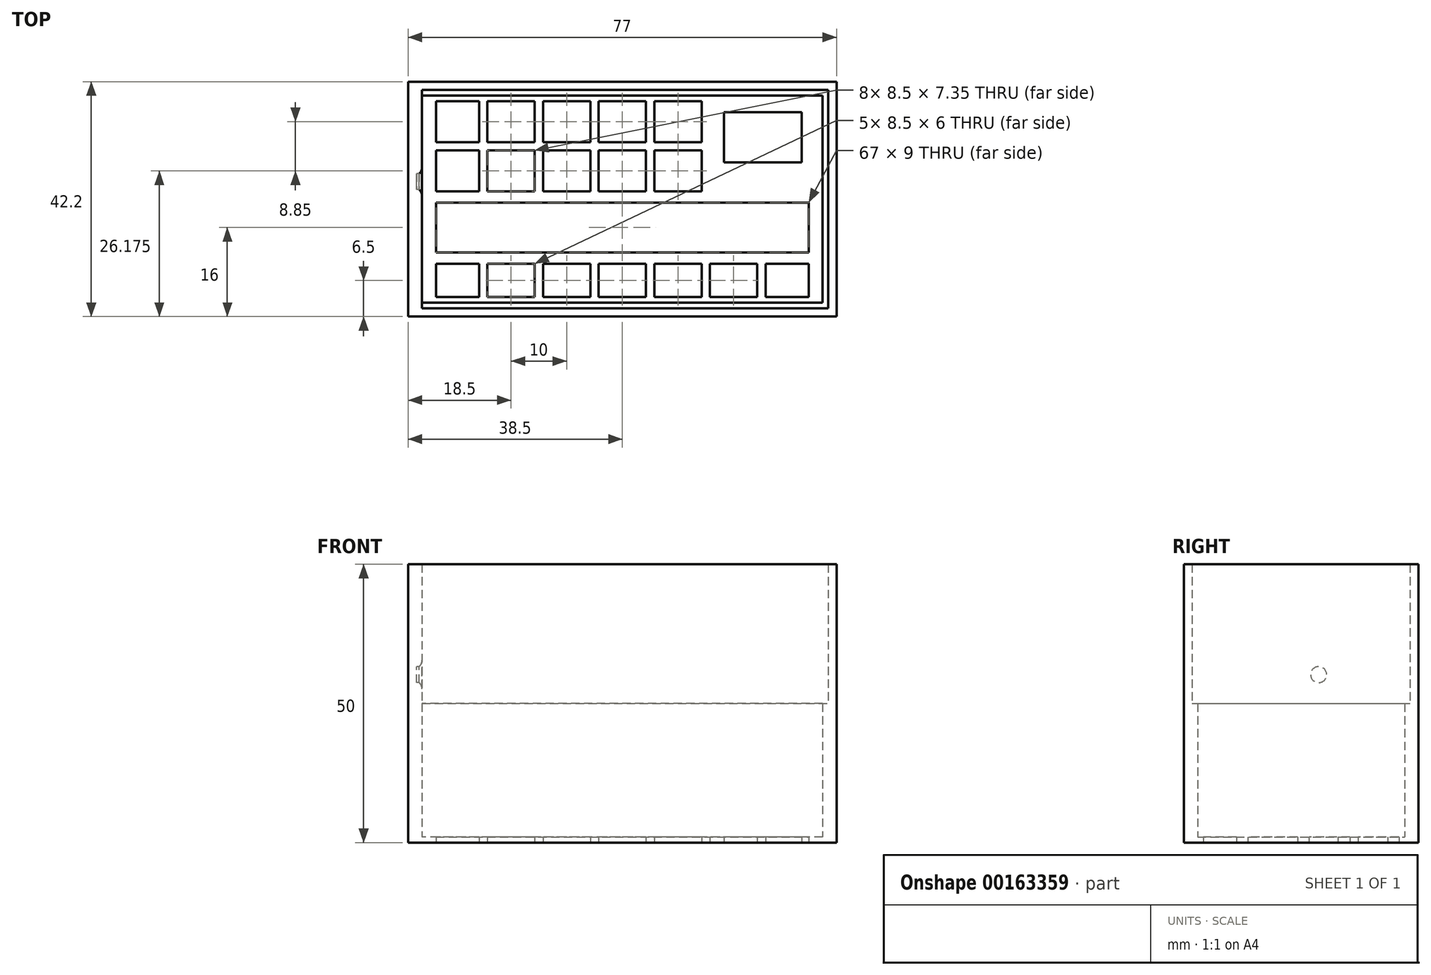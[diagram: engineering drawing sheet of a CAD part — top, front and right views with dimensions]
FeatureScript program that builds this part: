
annotation { "Feature Type Name" : "Feature", "Feature Type Description" : "" }
export const myFeature = defineFeature(function(context is Context, id is Id, definition is map)
    precondition{}
    {
        {
            var Q0;
            Q0=qCreatedBy(makeId("Top.planeOp"),FACE);
            var sketch = newSketch(context, id + "F0", { "sketchPlane" : qUnion([Q0])});
            skLineSegment(sketch, "E0.bottom", {"start": v(37, 18.6) * mm, "end": v(-37, 18.6) * mm});
            skLineSegment(sketch, "E0.top", {"start": v(37, -18.6) * mm, "end": v(-37, -18.6) * mm});
            skLineSegment(sketch, "E0.left", {"start": v(37, 18.6) * mm, "end": v(37, -18.6) * mm});
            skLineSegment(sketch, "E0.right", {"start": v(-37, 18.6) * mm, "end": v(-37, -18.6) * mm});
            skPoint(sketch, "E0.middle", {"position": v(0, 0) * mm});
            skLineSegment(sketch, "E1.1", {"start": v(38.5, 19.6) * mm, "end": v(38.5, -19.6) * mm});
            skLineSegment(sketch, "E1.3", {"start": v(-38.5, 19.6) * mm, "end": v(-38.5, -19.6) * mm});
            skLineSegment(sketch, "E2.2", {"start": v(33.5, -17.6) * mm, "end": v(25.75, -17.6) * mm});
            skLineSegment(sketch, "E3", {"start": v(-33.5, -9.6) * mm, "end": v(33.5, -9.6) * mm});
            skLineSegment(sketch, "E4", {"start": v(-33.5, -0.6) * mm, "end": v(33.5, -0.6) * mm});
            skLineSegment(sketch, "E5", {"start": v(-33.5, 17.6) * mm, "end": v(-33.5, 10.25) * mm});
            skLineSegment(sketch, "E6", {"start": v(0, 16.6) * mm, "end": v(0, -16.6) * mm, "construction": true});
            skLineSegment(sketch, "E7", {"start": v(-33.5, 1.4) * mm, "end": v(-25.75, 1.4) * mm});
            skLineSegment(sketch, "E8", {"start": v(33.5, -11.6) * mm, "end": v(25.75, -11.6) * mm});
            skLineSegment(sketch, "E9", {"start": v(-25.75, 17.6) * mm, "end": v(-25.75, 10.25) * mm});
            skLineSegment(sketch, "E10.trimOffspring", {"start": v(-25.75, -11.6) * mm, "end": v(-25.75, -17.6) * mm});
            skLineSegment(sketch, "E11", {"start": v(-24.25, 17.6) * mm, "end": v(-24.25, 10.25) * mm});
            skLineSegment(sketch, "E12.trimOffspring", {"start": v(-24.25, -11.6) * mm, "end": v(-24.25, -17.6) * mm});
            skPoint(sketch, "E13.orphan", {"position": v(-33.5, -0.6) * mm});
            skPoint(sketch, "E14.orphan", {"position": v(-33.5, -9.6) * mm});
            skPoint(sketch, "E15.orphan", {"position": v(33.5, -0.6) * mm});
            skPoint(sketch, "E16.orphan", {"position": v(33.5, -9.6) * mm});
            skLineSegment(sketch, "E17.trimOffspring", {"start": v(33.5, -11.6) * mm, "end": v(33.5, -17.6) * mm});
            skLineSegment(sketch, "E18.trimOffspring", {"start": v(33.5, -0.6) * mm, "end": v(33.5, -9.6) * mm});
            skLineSegment(sketch, "E19.trimOffspring", {"start": v(-33.5, -0.6) * mm, "end": v(-33.5, -9.6) * mm});
            skLineSegment(sketch, "E20.trimOffspring", {"start": v(-33.5, -11.6) * mm, "end": v(-33.5, -17.6) * mm});
            skLineSegment(sketch, "E21.1.0.0", {"start": v(-14.25, 17.6) * mm, "end": v(-14.25, 10.25) * mm});
            skLineSegment(sketch, "E21.1.0.1", {"start": v(-15.75, 17.6) * mm, "end": v(-15.75, 10.25) * mm});
            skLineSegment(sketch, "E21.1.0.2", {"start": v(-15.75, -11.6) * mm, "end": v(-15.75, -17.6) * mm});
            skLineSegment(sketch, "E21.1.0.3", {"start": v(-14.25, -11.6) * mm, "end": v(-14.25, -17.6) * mm});
            skLineSegment(sketch, "E21.2.0.0", {"start": v(-4.25, 17.6) * mm, "end": v(-4.25, 10.25) * mm});
            skLineSegment(sketch, "E21.2.0.1", {"start": v(-5.75, 17.6) * mm, "end": v(-5.75, 10.25) * mm});
            skLineSegment(sketch, "E21.2.0.2", {"start": v(-5.75, -11.6) * mm, "end": v(-5.75, -17.6) * mm});
            skLineSegment(sketch, "E21.2.0.3", {"start": v(-4.25, -11.6) * mm, "end": v(-4.25, -17.6) * mm});
            skLineSegment(sketch, "E21.3.0.0", {"start": v(5.75, 17.6) * mm, "end": v(5.75, 10.25) * mm});
            skLineSegment(sketch, "E21.3.0.1", {"start": v(4.25, 17.6) * mm, "end": v(4.25, 10.25) * mm});
            skLineSegment(sketch, "E21.3.0.2", {"start": v(4.25, -11.6) * mm, "end": v(4.25, -17.6) * mm});
            skLineSegment(sketch, "E21.3.0.3", {"start": v(5.75, -11.6) * mm, "end": v(5.75, -17.6) * mm});
            skLineSegment(sketch, "E21.4.0.1", {"start": v(14.25, 17.6) * mm, "end": v(14.25, 10.25) * mm});
            skLineSegment(sketch, "E21.4.0.2", {"start": v(14.25, -11.6) * mm, "end": v(14.25, -17.6) * mm});
            skLineSegment(sketch, "E21.4.0.3", {"start": v(15.75, -11.6) * mm, "end": v(15.75, -17.6) * mm});
            skLineSegment(sketch, "E21.5.0.2", {"start": v(24.25, -11.6) * mm, "end": v(24.25, -17.6) * mm});
            skLineSegment(sketch, "E21.5.0.3", {"start": v(25.75, -11.6) * mm, "end": v(25.75, -17.6) * mm});
            skLineSegment(sketch, "E21.direction1", {"start": v(-24.25, 1.4) * mm, "end": v(-14.25, 1.4) * mm, "construction": true});
            skPoint(sketch, "E22", {"position": v(0, -11.6) * mm});
            skLineSegment(sketch, "E23", {"start": v(-33.5, 10.25) * mm, "end": v(-25.75, 10.25) * mm});
            skLineSegment(sketch, "E24", {"start": v(-33.5, 8.75) * mm, "end": v(-25.75, 8.75) * mm});
            skLineSegment(sketch, "E25.trimOffspring", {"start": v(-25.75, -11.6) * mm, "end": v(-33.5, -11.6) * mm});
            skLineSegment(sketch, "E26.trimOffspring", {"start": v(-15.75, -11.6) * mm, "end": v(-24.25, -11.6) * mm});
            skLineSegment(sketch, "E27.trimOffspring", {"start": v(-5.75, -11.6) * mm, "end": v(-14.25, -11.6) * mm});
            skLineSegment(sketch, "E28.trimOffspring", {"start": v(4.25, -11.6) * mm, "end": v(-4.25, -11.6) * mm});
            skLineSegment(sketch, "E29.trimOffspring", {"start": v(14.25, -11.6) * mm, "end": v(5.75, -11.6) * mm});
            skLineSegment(sketch, "E30.trimOffspring", {"start": v(24.25, -11.6) * mm, "end": v(15.75, -11.6) * mm});
            skLineSegment(sketch, "E31.trimOffspring", {"start": v(5.75, 1.4) * mm, "end": v(14.25, 1.4) * mm});
            skLineSegment(sketch, "E32.trimOffspring", {"start": v(-4.25, 1.4) * mm, "end": v(4.25, 1.4) * mm});
            skLineSegment(sketch, "E33", {"start": v(-14.25, 1.4) * mm, "end": v(-5.75, 1.4) * mm});
            skLineSegment(sketch, "E34", {"start": v(-15.75, 1.4) * mm, "end": v(-14.25, 1.4) * mm, "construction": true});
            skLineSegment(sketch, "E35.trimOffspring", {"start": v(-24.25, 1.4) * mm, "end": v(-15.75, 1.4) * mm});
            skLineSegment(sketch, "E36.trimOffspring", {"start": v(-33.5, 8.75) * mm, "end": v(-33.5, 1.4) * mm});
            skLineSegment(sketch, "E37.trimOffspring", {"start": v(-25.75, 8.75) * mm, "end": v(-25.75, 1.4) * mm});
            skLineSegment(sketch, "E38.trimOffspring", {"start": v(-24.25, 8.75) * mm, "end": v(-24.25, 1.4) * mm});
            skLineSegment(sketch, "E39.trimOffspring", {"start": v(-15.75, 8.75) * mm, "end": v(-15.75, 1.4) * mm});
            skLineSegment(sketch, "E40.trimOffspring", {"start": v(-14.25, 8.75) * mm, "end": v(-14.25, 1.4) * mm});
            skLineSegment(sketch, "E41.trimOffspring", {"start": v(-5.75, 8.75) * mm, "end": v(-5.75, 1.4) * mm});
            skLineSegment(sketch, "E42.trimOffspring", {"start": v(-4.25, 8.75) * mm, "end": v(-4.25, 1.4) * mm});
            skLineSegment(sketch, "E43.trimOffspring", {"start": v(4.25, 8.75) * mm, "end": v(4.25, 1.4) * mm});
            skLineSegment(sketch, "E44.trimOffspring", {"start": v(5.75, 8.75) * mm, "end": v(5.75, 1.4) * mm});
            skLineSegment(sketch, "E45.trimOffspring", {"start": v(14.25, 8.75) * mm, "end": v(14.25, 1.4) * mm});
            skLineSegment(sketch, "E46.trimOffspring", {"start": v(-24.25, 10.25) * mm, "end": v(-15.75, 10.25) * mm});
            skLineSegment(sketch, "E47.trimOffspring", {"start": v(-24.25, 8.75) * mm, "end": v(-15.75, 8.75) * mm});
            skLineSegment(sketch, "E48.trimOffspring", {"start": v(-14.25, 10.25) * mm, "end": v(-5.75, 10.25) * mm});
            skLineSegment(sketch, "E49.trimOffspring", {"start": v(-14.25, 8.75) * mm, "end": v(-5.75, 8.75) * mm});
            skLineSegment(sketch, "E50.trimOffspring", {"start": v(-4.25, 10.25) * mm, "end": v(4.25, 10.25) * mm});
            skLineSegment(sketch, "E51.trimOffspring", {"start": v(-4.25, 8.75) * mm, "end": v(4.25, 8.75) * mm});
            skLineSegment(sketch, "E52.trimOffspring", {"start": v(5.75, 10.25) * mm, "end": v(14.25, 10.25) * mm});
            skLineSegment(sketch, "E53.trimOffspring", {"start": v(5.75, 8.75) * mm, "end": v(14.25, 8.75) * mm});
            skLineSegment(sketch, "E54.trimOffspring", {"start": v(-25.75, 17.6) * mm, "end": v(-33.5, 17.6) * mm});
            skLineSegment(sketch, "E55.trimOffspring", {"start": v(-15.75, 17.6) * mm, "end": v(-24.25, 17.6) * mm});
            skLineSegment(sketch, "E56.trimOffspring", {"start": v(-5.75, 17.6) * mm, "end": v(-14.25, 17.6) * mm});
            skLineSegment(sketch, "E57.trimOffspring", {"start": v(4.25, 17.6) * mm, "end": v(-4.25, 17.6) * mm});
            skLineSegment(sketch, "E58.trimOffspring", {"start": v(14.25, 17.6) * mm, "end": v(5.75, 17.6) * mm});
            skLineSegment(sketch, "E59.trimOffspring", {"start": v(-25.75, -17.6) * mm, "end": v(-33.5, -17.6) * mm});
            skLineSegment(sketch, "E60.trimOffspring", {"start": v(-15.75, -17.6) * mm, "end": v(-24.25, -17.6) * mm});
            skLineSegment(sketch, "E61.trimOffspring", {"start": v(-5.75, -17.6) * mm, "end": v(-14.25, -17.6) * mm});
            skLineSegment(sketch, "E62.trimOffspring", {"start": v(4.25, -17.6) * mm, "end": v(-4.25, -17.6) * mm});
            skLineSegment(sketch, "E63.trimOffspring", {"start": v(14.25, -17.6) * mm, "end": v(5.75, -17.6) * mm});
            skLineSegment(sketch, "E64.trimOffspring", {"start": v(24.25, -17.6) * mm, "end": v(15.75, -17.6) * mm});
            skLineSegment(sketch, "E65", {"start": v(-38.5, 19.6) * mm, "end": v(38.5, 19.6) * mm});
            skLineSegment(sketch, "E66", {"start": v(-38.5, -19.6) * mm, "end": v(38.5, -19.6) * mm});
            skLineSegment(sketch, "E67", {"start": v(-37, 18.6) * mm, "end": v(-37, 19.6) * mm});
            skLineSegment(sketch, "E68", {"start": v(-37, -18.6) * mm, "end": v(-37, -19.6) * mm});
            skLineSegment(sketch, "E69", {"start": v(37, -18.6) * mm, "end": v(37, -19.6) * mm});
            skLineSegment(sketch, "E70", {"start": v(37, 18.6) * mm, "end": v(37, 19.6) * mm});
            skLineSegment(sketch, "E71.bottom", {"start": v(32.25, 6.6) * mm, "end": v(18.25, 6.6) * mm});
            skLineSegment(sketch, "E71.top", {"start": v(32.25, 15.6) * mm, "end": v(18.25, 15.6) * mm});
            skLineSegment(sketch, "E71.left", {"start": v(32.25, 6.6) * mm, "end": v(32.25, 15.6) * mm});
            skLineSegment(sketch, "E71.right", {"start": v(18.25, 6.6) * mm, "end": v(18.25, 15.6) * mm});
            skPoint(sketch, "E71.middle", {"position": v(25.25, 11.1) * mm});
            skLineSegment(sketch, "E72", {"start": v(-38.5, 19.6) * mm, "end": v(-38.5, 21.1) * mm});
            skLineSegment(sketch, "E73", {"start": v(-38.5, 21.1) * mm, "end": v(38.5, 21.1) * mm});
            skLineSegment(sketch, "E74", {"start": v(38.5, 21.1) * mm, "end": v(38.5, 19.6) * mm});
            skLineSegment(sketch, "E75", {"start": v(-38.5, -19.6) * mm, "end": v(-38.5, -21.1) * mm});
            skLineSegment(sketch, "E76", {"start": v(-38.5, -21.1) * mm, "end": v(38.5, -21.1) * mm});
            skLineSegment(sketch, "E77", {"start": v(38.5, -21.1) * mm, "end": v(38.5, -19.6) * mm});
            skLineSegment(sketch, "E78", {"start": v(-36, 18.6) * mm, "end": v(-36, -18.6) * mm});
            skLineSegment(sketch, "E79", {"start": v(36, -18.6) * mm, "end": v(36, 18.6) * mm});
            skSolve(sketch);
        }
        {
            var Q0;
            Q0=makeQuery(id+"F0.imprint","IMPRINT",FACE,{"disambiguationData":[TD([[makeQuery(id+"F0.imprint","IMPRINT",EDGE,{"derivedFrom":sQuery(id+"F0.wireOp",EDGE,"E2.2")}),1.0]])]});
            extrude(context, id + "F1", {"entities" : qUnion([Q0]), "depth" : 1 * mm});
        }
        {
            var Q0;
            Q0=makeQuery(id+"F0.imprint","IMPRINT",FACE,{"disambiguationData":[TD([[makeQuery(id+"F0.imprint","IMPRINT",EDGE,{"derivedFrom":sQuery(id+"F0.wireOp",EDGE,"E0.bottom")}),-1.0]])]});
            var Q1;
            Q1=makeQuery(id+"F0.imprint","IMPRINT",FACE,{"disambiguationData":[TD([[makeQuery(id+"F0.imprint","IMPRINT",EDGE,{"derivedFrom":sQuery(id+"F0.wireOp",EDGE,"E0.top")}),1.0]])]});
            var Q2;
            {var subQ0=sQuery(id+"F0.wireOp",EDGE,"E0.right");Q2=makeQuery(id+"F0.imprint","IMPRINT",FACE,{"disambiguationData":[TD([[makeQuery(id+"F0.imprint","IMPRINT",EDGE,{"derivedFrom":subQ0}),1.0]])]});}
            var Q3;
            {var subQ0=sQuery(id+"F0.wireOp",EDGE,"E0.left");Q3=makeQuery(id+"F0.imprint","IMPRINT",FACE,{"disambiguationData":[TD([[makeQuery(id+"F0.imprint","IMPRINT",EDGE,{"derivedFrom":subQ0}),-1.0]])]});}
            extrude(context, id + "F2", {"entities" : qUnion([Q0, Q1, Q2, Q3]), "operationType" : NewBodyOperationType.ADD, "depth" : 25 * mm});
        }
        {
            var Q0;
            {var subQ0=sQuery(id+"F0.wireOp",EDGE,"E75");Q0=makeQuery(id+"F0.imprint","IMPRINT",FACE,{"disambiguationData":[TD([[makeQuery(id+"F0.imprint","IMPRINT",EDGE,{"derivedFrom":subQ0}),1.0]])]});}
            var Q1;
            Q1=makeQuery(id+"F0.imprint","IMPRINT",FACE,{"disambiguationData":[TD([[makeQuery(id+"F0.imprint","IMPRINT",EDGE,{"derivedFrom":sQuery(id+"F0.wireOp",EDGE,"E0.right")}),-1.0]])]});
            var Q2;
            Q2=makeQuery(id+"F0.imprint","IMPRINT",FACE,{"disambiguationData":[TD([[makeQuery(id+"F0.imprint","IMPRINT",EDGE,{"derivedFrom":sQuery(id+"F0.wireOp",EDGE,"E0.left")}),1.0]])]});
            var Q3;
            {var subQ3=sQuery(id+"F0.wireOp",EDGE,"E72");Q3=makeQuery(id+"F0.imprint","IMPRINT",FACE,{"disambiguationData":[TD([[makeQuery(id+"F0.imprint","IMPRINT",EDGE,{"derivedFrom":subQ3}),-1.0]])]});}
            extrude(context, id + "F3", {"entities" : qUnion([Q0, Q1, Q2, Q3]), "operationType" : NewBodyOperationType.ADD, "depth" : 50 * mm});
        }
        {
            var Q0;
            Q0=makeQuery(id+"F3.opExtrude","SWEPT_FACE",FACE,{"disambiguationData":[OSD([sQuery(id+"F0.wireOp",EDGE,"E1.3"),sQuery(id+"F0.wireOp",EDGE,"E72"),sQuery(id+"F0.wireOp",EDGE,"E75")])]});
            var sketch = newSketch(context, id + "F4", { "sketchPlane" : qUnion([Q0])});
            skCircle(sketch, "E80", {"center": v(-3.15, 30.17) * mm, "radius": 1.45 * mm});
            skLineSegment(sketch, "E81.0", {"start": v(-19.6, 25) * mm, "end": v(-19.6, 25) * mm});
            skLineSegment(sketch, "E82.0", {"start": v(-19.6, 50) * mm, "end": v(-19.6, 25) * mm});
            skLineSegment(sketch, "E83.0", {"start": v(19.6, 25) * mm, "end": v(-19.6, 25) * mm});
            skCircle(sketch, "E84", {"center": v(-3.15, 30.17) * mm, "radius": 5.17 * mm, "construction": true});
            skSolve(sketch);
        }
        {
            var Q0;
            Q0=makeQuery(id+"F3.opExtrude","SWEPT_FACE",FACE,{"disambiguationData":[OSD([sQuery(id+"F0.wireOp",EDGE,"E0.right"),sQuery(id+"F0.wireOp",EDGE,"E67"),sQuery(id+"F0.wireOp",EDGE,"E68")])]});
            var sketch = newSketch(context, id + "F5", { "sketchPlane" : qUnion([Q0])});
            skCircle(sketch, "E85.0", {"center": v(3.15, 30.17) * mm, "radius": 1.45 * mm});
            skSolve(sketch);
        }
        {
            var Q0;
            Q0=makeQuery(id+"F5.imprint","IMPRINT",FACE,{"disambiguationData":[TD([[makeQuery(id+"F5.imprint","IMPRINT",EDGE,{"derivedFrom":sQuery(id+"F5.wireOp",EDGE,"E85.0")}),-1.0]])]});
            var Q1;
            Q1=sQuery(id+"F5.wireOp",EDGE,"E85.0");
            extrude(context, id + "F6", {"entities" : qUnion([Q0]), "operationType" : NewBodyOperationType.ADD, "surfaceEntities" : qUnion([Q1]), "depth" : 1 * mm});
        }
        {
            var Q0;
            Q0=makeQuery(id+"F6.opExtrude","CAP_EDGE",EDGE,{"disambiguationData":[OSD([sQuery(id+"F5.wireOp",EDGE,"E85.0")])],"isStart":false});
            chamfer(context, id + "F7", {"entities" : qUnion([Q0]), "width" : 0.5 * mm, "tangentPropagation" : true});
        }
        {
            var Q0;
            {var subQ0=sQuery(id+"F5.wireOp",EDGE,"E85.0");Q0=makeQuery(id+"F7.opChamfer","BLEND_EDGE",EDGE,{"blendedFrom":[makeQuery(id+"F6.opExtrude","CAP_EDGE",EDGE,{"disambiguationData":[OSD([subQ0])],"isStart":false}),makeQuery(id+"F6.opExtrude","CAP_FACE",FACE,{"disambiguationData":[OSD([subQ0])],"isStart":false})],"blendedInto":[makeQuery(id+"F6.opExtrude","CAP_FACE",FACE,{"disambiguationData":[OSD([subQ0])],"isStart":false})]});}
            fillet(context, id + "F8", {"entities" : qUnion([Q0]), "radius" : 1.5 * mm, "tangentPropagation" : true, "allowEdgeOverflow" : false});
        }
    });
